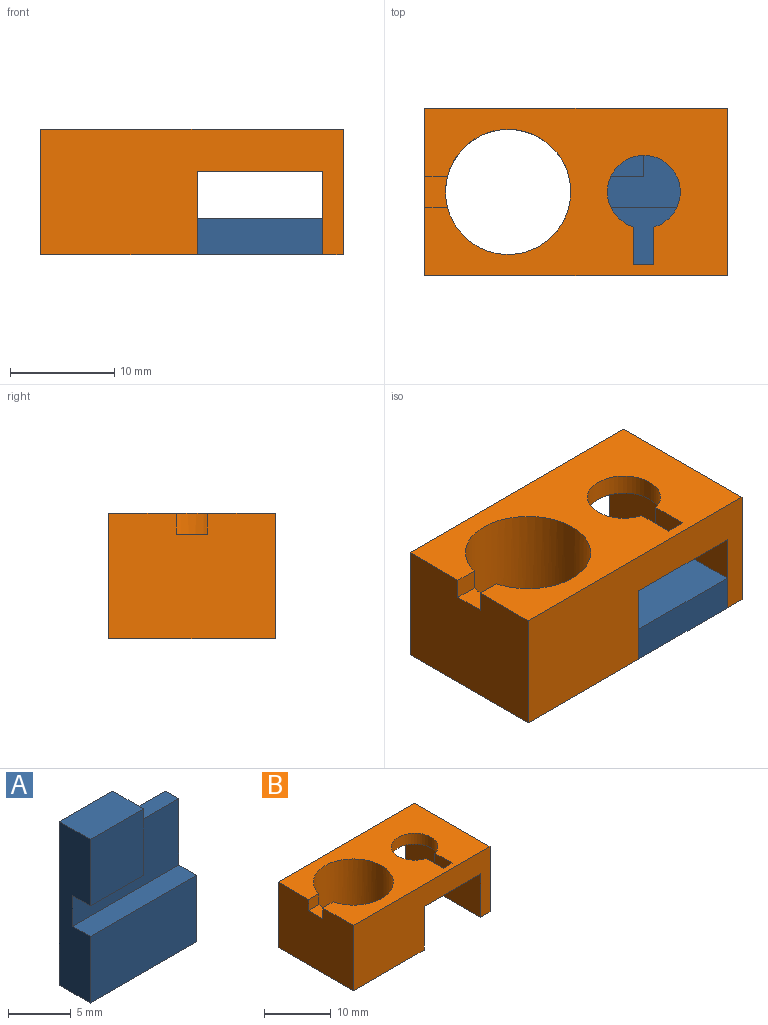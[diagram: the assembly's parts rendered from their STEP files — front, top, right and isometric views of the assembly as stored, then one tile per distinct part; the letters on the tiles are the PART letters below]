
ASSEMBLY  parts=2 mates=1
PART A: 12 faces, bbox 12x3.5x16 mm
  f0: plane 6x1.5mm, normal (0,0,1), area 9mm2, adj f1,f6,f8,f11
  f1: plane 13x3.5mm, normal (1,0,0), area 32.5mm2, adj f0,f4,f7,f8,f10,f11
  f2: plane 16x3.5mm, normal (-1,0,0), area 50mm2, adj f3,f4,f5,f7,f8,f9,f10,f11
  f3: plane 6.5x6mm, normal (0,-1,0), area 39mm2, adj f2,f5,f6,f9
  f4: plane 12x3.5mm, normal (0,0,-1), area 42mm2, adj f1,f2,f7,f8
  f5: plane 6x3.5mm, normal (0,0,1), area 21mm2, adj f2,f3,f6,f8
  f6: plane 6.5x3.5mm, normal (1,0,0), area 17.5mm2, adj f0,f3,f5,f8,f9,f11
  f7: plane 12x6.5mm, normal (0,-1,0), area 78mm2, adj f1,f2,f4,f10
  f8: plane 16x12mm, normal (0,1,0), area 174mm2, adj f0,f1,f2,f4,f5,f6
  f9: plane 6x2mm, normal (0,0,-1), area 12mm2, adj f2,f3,f6,f11
  f10: plane 12x2mm, normal (0,0,1), area 24mm2, adj f1,f2,f7,f11
  f11: plane 12x6.5mm, normal (0,-1,0), area 57mm2, adj f0,f1,f2,f6,f9,f10
PART B: 21 faces, bbox 29x16x12 mm
  f0: plane 12x1mm, normal (0,0,-1), area 12mm2, adj f2,f8,f14,f15
  f1: plane 16x12mm, normal (-1,0,0), area 186mm2, adj f2,f4,f5,f11,f12,f18,f20
  f2: plane 29x12mm, normal (0,-1,0), area 252mm2, adj f0,f1,f3,f12,f14,f15,f19,f20
  f3: plane 16x12mm, normal (1,0,0), area 192mm2, adj f2,f4,f12,f19
  f4: plane 29x12mm, normal (0,1,0), area 252mm2, adj f1,f3,f12,f14,f15,f17,f19,f20
  f5: plane 2.19x2mm, normal (0,-1,0), area 4.4mm2, adj f1,f6,f12,f18
  f6: cylinder r=6mm len=12mm, axis (0,0,-1), area 446.3mm2, adj f5,f11,f12,f18,f20
  f7: plane 3.63x2mm, normal (-1,0,0), area 7.3mm2, adj f8,f10,f12,f13
  f8: plane 12x4mm, normal (0,1,0), area 27.8mm2, adj f0,f7,f9,f12,f13,f14,f15
  f9: plane 3.63x2mm, normal (1,0,0), area 7.3mm2, adj f8,f10,f12,f13
  f10: cylinder r=3.5mm len=7mm, axis (0,0,-1), area 40.1mm2, adj f7,f9,f12,f13
  f11: plane 2.19x2mm, normal (0,1,0), area 4.4mm2, adj f1,f6,f12,f18
  f12: plane 29x16mm, normal (0,0,1), area 299.5mm2, adj f1,f2,f3,f4,f5,f6,f7,f8
  f13: plane 14x12mm, normal (0,0,-1), area 122.8mm2, adj f7,f8,f9,f10,f14,f15,f16
  f14: plane 16x10mm, normal (-1,0,0), area 156mm2, adj f0,f2,f4,f8,f13,f16,f17,f19
  f15: plane 16x10mm, normal (1,0,0), area 156mm2, adj f0,f2,f4,f8,f13,f16,f17,f20
  f16: plane 12x2mm, normal (0,-1,0), area 24mm2, adj f13,f14,f15,f17
  f17: plane 12x1mm, normal (0,0,-1), area 12mm2, adj f4,f14,f15,f16
  f18: plane 3x2.19mm, normal (0,0,1), area 6.2mm2, adj f1,f5,f6,f11
  f19: plane 16x2mm, normal (0,0,-1), area 32mm2, adj f2,f3,f4,f14
  f20: plane 16x15mm, normal (0,0,-1), area 126.9mm2, adj f1,f2,f4,f6,f15
PLACE A rot(axis=(-1,0,0),90deg) t=(0.5,0,-10)mm
PLACE B at identity fixed
MATE fastened B.f20 <-> A.f8  axis (0,0,-1) through (0.5,0,-10)mm
